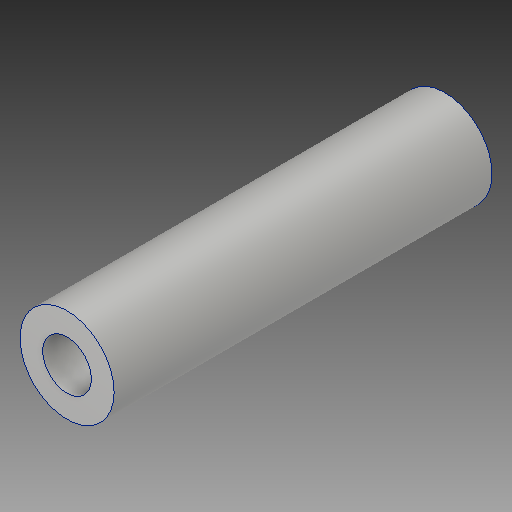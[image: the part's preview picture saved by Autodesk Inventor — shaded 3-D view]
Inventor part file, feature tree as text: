
AUTODESK INVENTOR PART (.ipt)
format: ipt  version: 2017 (Build 210142000, 142)  size: 99,328 bytes
history: native  units: in
note: dims shown in document units (in); Inventor stores cm internally (conversion verified against a paired STEP export)
features: extrude x1, sketch x1
ambient origin geometry x8: Origin, YZ Plane, XZ Plane, XY Plane, X Axis, Y Axis, Z Axis, Center Point
bodies: Solid1 (feature_tree)
feature tree (2):
  extrude  "Extrusion1"  [1 undecoded]
  sketch  "Sketch1"  dims[d0=2.0in d1=0.0in]
note: 1 required parameter value undecoded (feature->parameter linkage not recoverable at this tier; creation-order binding heuristic only, values carry confidence <= 0.55)
